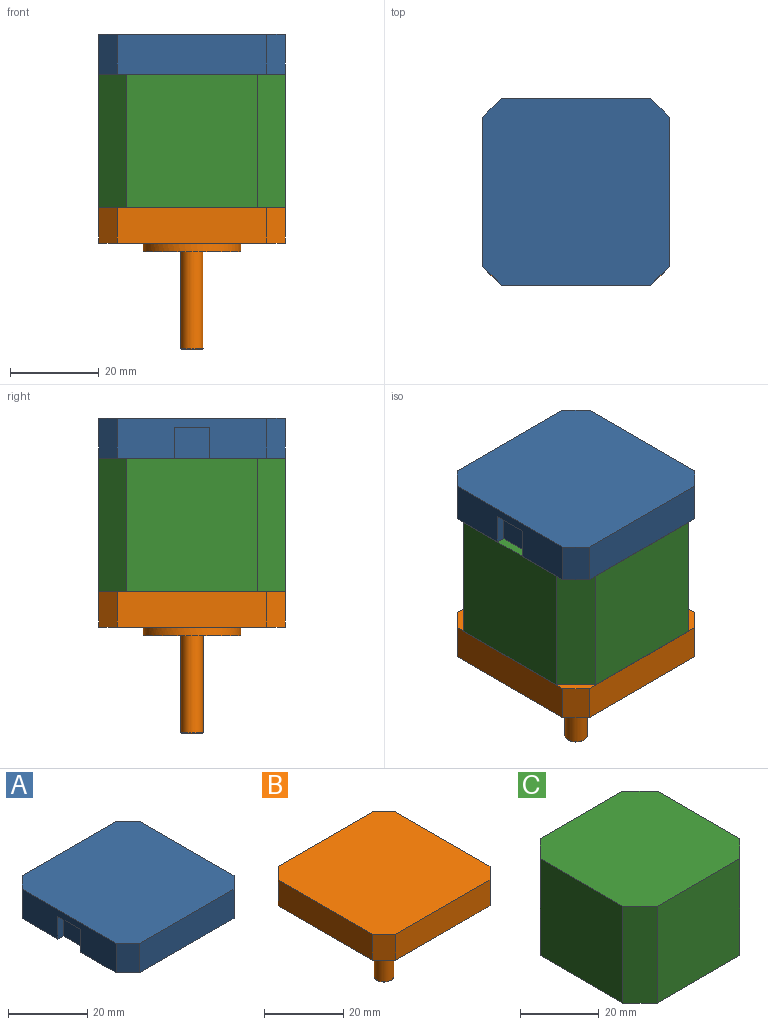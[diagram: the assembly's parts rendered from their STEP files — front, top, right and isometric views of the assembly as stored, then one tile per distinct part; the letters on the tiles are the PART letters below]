
ASSEMBLY  parts=3 mates=2
PART A: 14 faces, bbox 42x42x9 mm
  f0: plane 33.6x9mm, normal (1,0,0), area 302.4mm2, adj f4,f5,f6,f7
  f1: plane 33.6x9mm, normal (0,1,0), area 302.4mm2, adj f4,f5,f6,f9
  f2: plane 33.6x9mm, normal (-1,0,0), area 246.4mm2, adj f4,f5,f8,f9,f10,f11,f12
  f3: plane 33.6x9mm, normal (0,-1,0), area 302.4mm2, adj f4,f5,f7,f8
  f4: plane 42x42mm, normal (0,0,1), area 1728.7mm2, adj f0,f1,f2,f3,f6,f7,f8,f9
  f5: plane 42x42mm, normal (0,0,-1), area 1712.7mm2, adj f0,f1,f2,f3,f6,f7,f8,f9
  f6: plane 9x4.2mm, normal (0.71,0.71,0), area 53.5mm2, adj f0,f1,f4,f5
  f7: plane 9x4.2mm, normal (0.71,-0.71,0), area 53.5mm2, adj f0,f3,f4,f5
  f8: plane 9x4.2mm, normal (-0.71,-0.71,0), area 53.5mm2, adj f2,f3,f4,f5
  f9: plane 9x4.2mm, normal (-0.71,0.71,0), area 53.5mm2, adj f1,f2,f4,f5
  f10: plane 8x2mm, normal (0,0,-1), area 16mm2, adj f2,f11,f12,f13
  f11: plane 7x2mm, normal (0,1,0), area 14mm2, adj f2,f5,f10,f13
  f12: plane 7x2mm, normal (0,-1,0), area 14mm2, adj f2,f5,f10,f13
  f13: plane 8x7mm, normal (-1,0,0), area 56mm2, adj f5,f10,f11,f12
PART B: 29 faces, bbox 42x42x32 mm
  f0: plane 9x9mm, normal (0,0,-1), area 44mm2, adj f13,f14
  f1: plane 42x42mm, normal (0,0,-1), area 1312.3mm2, adj f2,f3,f4,f5,f7,f8,f9,f10
  f2: plane 33.6x8mm, normal (1,0,0), area 268.8mm2, adj f1,f6,f9,f10
  f3: plane 33.6x8mm, normal (0,1,0), area 268.8mm2, adj f1,f6,f8,f9
  f4: plane 33.6x8mm, normal (-1,0,0), area 268.8mm2, adj f1,f6,f7,f8
  f5: plane 33.6x8mm, normal (0,-1,0), area 268.8mm2, adj f1,f6,f7,f10
  f6: plane 42x42mm, normal (0,0,1), area 1728.7mm2, adj f2,f3,f4,f5,f7,f8,f9,f10
  f7: plane 8x4.2mm, normal (-0.71,-0.71,0), area 47.5mm2, adj f1,f4,f5,f6
  f8: plane 8x4.2mm, normal (-0.71,0.71,0), area 47.5mm2, adj f1,f3,f4,f6
  f9: plane 8x4.2mm, normal (0.71,0.71,0), area 47.5mm2, adj f1,f2,f3,f6
  f10: plane 8x4.2mm, normal (0.71,-0.71,0), area 47.5mm2, adj f1,f2,f5,f6
  f11: cylinder r=11mm len=22mm, axis (0,0,1), area 138.2mm2, adj f1,f12
  f12: plane 22x22mm, normal (0,0,-1), area 316.5mm2, adj f11,f13
  f13: cylinder r=4.5mm len=9mm, axis (0,0,-1), area 84.8mm2, adj f0,f12
  f14: cylinder r=2.5mm len=24.8mm, axis (0,0,1), area 389.6mm2, adj f0,f16
  f15: plane 4.6x4.6mm, normal (0,0,-1), area 16.6mm2, adj f16
  f16: cone r=2.3mm half-angle=45deg, axis (0,0,1), area 4.3mm2, adj f14,f15
  f17: cylinder r=1.5mm len=4.8mm, axis (0,0,-1), area 45.2mm2, adj f18,f28
  f18: plane 3x3mm, normal (0,0,-1), area 7.1mm2, adj f17
  f19: cylinder r=1.5mm len=4.8mm, axis (0,0,-1), area 45.2mm2, adj f20,f27
  f20: plane 3x3mm, normal (0,0,-1), area 7.1mm2, adj f19
  f21: cylinder r=1.5mm len=4.8mm, axis (0,0,-1), area 45.2mm2, adj f22,f26
  f22: plane 3x3mm, normal (0,0,-1), area 7.1mm2, adj f21
  f23: cylinder r=1.5mm len=4.8mm, axis (0,0,-1), area 45.2mm2, adj f24,f25
  f24: plane 3x3mm, normal (0,0,-1), area 7.1mm2, adj f23
  f25: cone r=1.5mm half-angle=45deg, axis (0,0,-1), area 2.8mm2, adj f1,f23
  f26: cone r=1.5mm half-angle=45deg, axis (0,0,-1), area 2.8mm2, adj f1,f21
  f27: cone r=1.5mm half-angle=45deg, axis (0,0,-1), area 2.8mm2, adj f1,f19
  f28: cone r=1.5mm half-angle=45deg, axis (0,0,-1), area 2.8mm2, adj f1,f17
PART C: 10 faces, bbox 42x42x30 mm
  f0: plane 30x29.6mm, normal (0,1,0), area 888mm2, adj f1,f7,f8,f9
  f1: plane 30x6.2mm, normal (-0.71,0.71,0), area 263mm2, adj f0,f2,f8,f9
  f2: plane 30x29.6mm, normal (-1,0,0), area 888mm2, adj f1,f3,f8,f9
  f3: plane 30x6.2mm, normal (-0.71,-0.71,0), area 263mm2, adj f2,f4,f8,f9
  f4: plane 30x29.6mm, normal (0,-1,0), area 888mm2, adj f3,f5,f8,f9
  f5: plane 30x6.2mm, normal (0.71,-0.71,0), area 263mm2, adj f4,f6,f8,f9
  f6: plane 30x29.6mm, normal (1,0,0), area 888mm2, adj f5,f7,f8,f9
  f7: plane 30x6.2mm, normal (0.71,0.71,0), area 263mm2, adj f0,f6,f8,f9
  f8: plane 42x42mm, normal (0,0,1), area 1687.1mm2, adj f0,f1,f2,f3,f4,f5,f6,f7
  f9: plane 42x42mm, normal (0,0,-1), area 1687.1mm2, adj f0,f1,f2,f3,f4,f5,f6,f7
PLACE A t=(10.34,-2.63,14.85)mm
PLACE B t=(10.34,-2.63,14.85)mm
PLACE C t=(10.34,-2.63,14.85)mm
MATE fastened C.f8 <-> A.f5  axis (0,0,1) through (10.34,-23.63,52.85)mm
MATE fastened B.f6 <-> C.f9  axis (0,0,1) through (10.34,-23.63,22.85)mm
